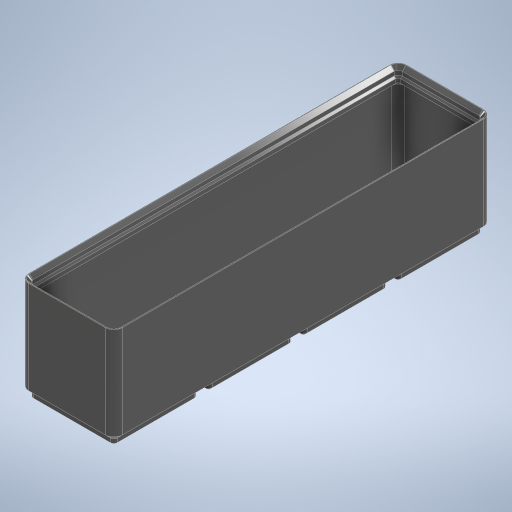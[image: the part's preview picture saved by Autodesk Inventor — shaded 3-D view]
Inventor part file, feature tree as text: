
AUTODESK INVENTOR PART (.ipt)
format: ipt  version: 2023 (Build 270158030, 158C)  size: 520,192 bytes
history: native  units: mm
features: extrude x14, sketch x14, projected_geometry x10, pattern_linear x1, fillet x1
ambient origin geometry x8: Origin, YZ Plane, XZ Plane, XY Plane, X Axis, Y Axis, Z Axis, Center Point
bodies: Solid2 (feature_tree)
feature tree (40):
  extrude  "base-generic"  Depth=41.5mm
  extrude  "Extrusion8"  Depth=3.75mm TaperAngle=0.0deg
  extrude  "Extrusion9"  Depth=2.15mm
  extrude  "Extrusion10"  Depth=0.8mm
  extrude  "Extrusion11"  Depth=7.75mm
  extrude  "Extrusion12"  Depth=7.75mm
  pattern_linear  "Rectangular Pattern1"  Count1=4 Spacing1=42.0mm
  extrude  "fill-gaps"  Depth=3.75mm
  extrude  "Extrusion14"  Depth=1.9mm
  extrude  "Extrusion15"  Depth=0.7mm
  extrude  "Extrusion16"  Depth=1.8mm TaperAngle=45.0deg
  extrude  "Extrusion17"  Depth=0.2mm TaperAngle=0.0deg
  extrude  "Extrusion18"  Depth=0.2mm
  extrude  "Extrusion19"  Depth=0.2mm
  extrude  "Extrusion20"  Depth=0.2mm
  fillet  "Fillet4"  Radius=0.5mm
  sketch  "Sketch9"  dims[d50=41.5mm d51=41.5mm]
  sketch  "Sketch10"  dims[d52=3.75mm d53=2.25mm d54=0.0mm]
  projected_geometry  "Projected Loop2"
  sketch  "Sketch11"  dims[d55=3.75mm d56=2.15mm d57=-7.853982mm]
  projected_geometry  "Projected Loop3"
  sketch  "Sketch12"  dims[d58=1.8mm d59=0.0mm d60=0.8mm d61=-7.853982mm]
  projected_geometry  "Projected Loop4"
  sketch  "Sketch13"  dims[d62=6.5mm d63=7.75mm]
  sketch  "Sketch14"  dims[d64=7.75mm d65=7.75mm]
  sketch  "Sketch15"  dims[d66=7.75mm]
  sketch  "Sketch16"  dims[d67=2.4mm d68=0.0mm]
  projected_geometry  "Projected Loop5"
  sketch  "Sketch19"  dims[d69=3.0mm]
  projected_geometry  "Projected Loop8"
  sketch  "Sketch20"  dims[d70=6.0mm d71=0.0mm d72=40.0mm d74=42.0mm d75=10.0mm d77=42.0mm]
  projected_geometry  "Projected Loop9"
  sketch  "Sketch21"  dims[d79=2.25mm d80=0.0mm d82=3.75mm]
  projected_geometry  "Projected Loop10"
  sketch  "Sketch22"  dims[d83=39.4mm d84=0.0mm d87=1.9mm d88=-7.853982mm]
  projected_geometry  "Projected Loop11"
  sketch  "Sketch23"  dims[d89=1.8mm d90=0.0mm d91=0.7mm d92=-7.853982mm]
  projected_geometry  "Projected Loop12"
  sketch  "Sketch24"  dims[d93=1.8mm d94=0.0mm d95=1.8mm d96=45.0deg d97=33.0mm d98=0.0mm d99=0.2mm d17=0.5mm d18=0.872665mm d19=0.5mm d20=0.872665mm d24=0.0mm d25=0.0mm d26=0.0mm d27=0.0mm]
  projected_geometry  "Projected Loop13"
